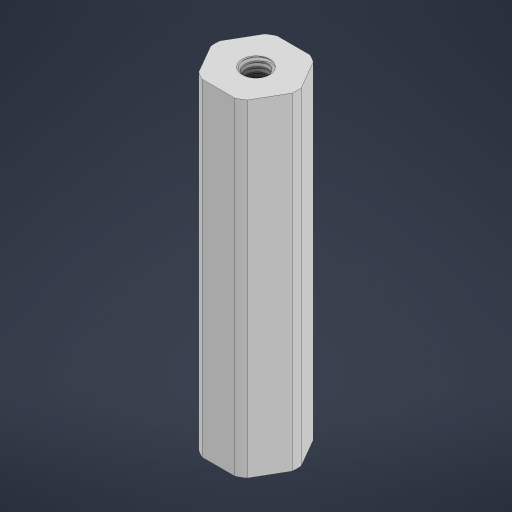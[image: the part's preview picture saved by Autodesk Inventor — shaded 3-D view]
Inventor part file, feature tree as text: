
AUTODESK INVENTOR PART (.ipt)
format: ipt  version: 2023 (Build 270158000, 158)  size: 1,019,392 bytes
history: native  units: in
note: dims shown in document units (in); Inventor stores cm internally (conversion verified against a paired STEP export)
features: mirror x1
ambient origin geometry x8: Origin, YZ Plane, XZ Plane, XY Plane, X Axis, Y Axis, Z Axis, Center Point
bodies: Solid1 (feature_tree)
feature tree (1):
  mirror  "Mirror2"
